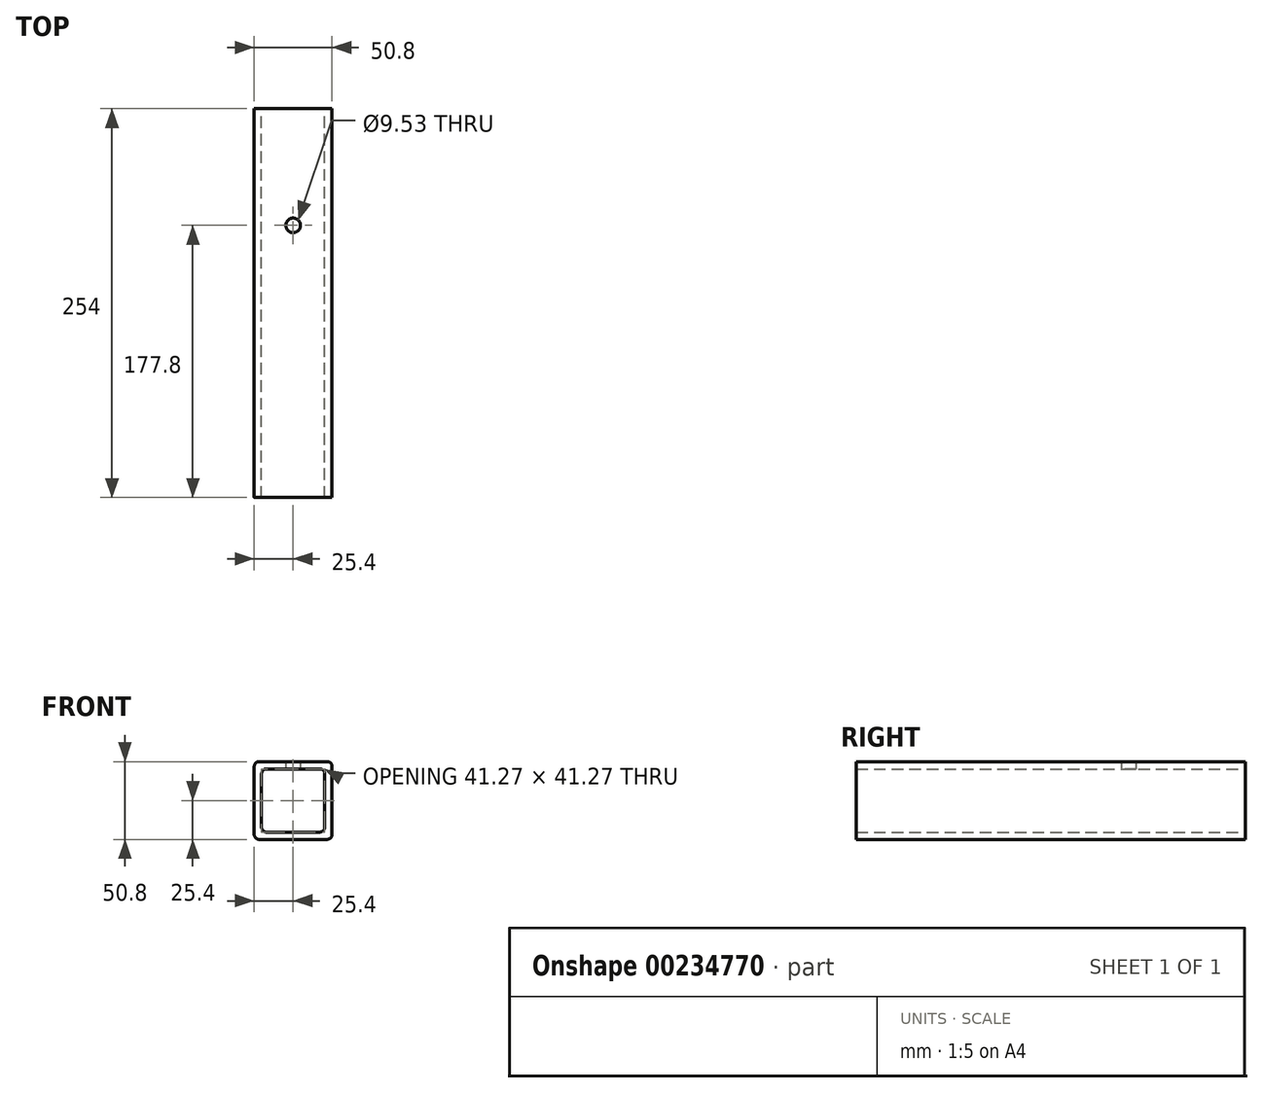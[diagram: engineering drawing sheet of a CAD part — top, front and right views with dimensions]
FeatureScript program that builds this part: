
annotation { "Feature Type Name" : "Feature", "Feature Type Description" : "" }
export const myFeature = defineFeature(function(context is Context, id is Id, definition is map)
    precondition{}
    {
        {
            var Q0;
            Q0=qCreatedBy(makeId("Front.planeOp"),FACE);
            var sketch = newSketch(context, id + "F0", { "sketchPlane" : qUnion([Q0])});
            skLineSegment(sketch, "E0.bottom", {"start": v(22.23, -25.4) * mm, "end": v(-22.23, -25.4) * mm});
            skLineSegment(sketch, "E0.top", {"start": v(22.23, 25.4) * mm, "end": v(-22.23, 25.4) * mm});
            skLineSegment(sketch, "E0.left", {"start": v(25.4, -22.23) * mm, "end": v(25.4, 22.23) * mm});
            skLineSegment(sketch, "E0.right", {"start": v(-25.4, -22.23) * mm, "end": v(-25.4, 22.23) * mm});
            skPoint(sketch, "E0.middle", {"position": v(0, 0) * mm});
            skLineSegment(sketch, "E1.bottom", {"start": v(17.46, -20.64) * mm, "end": v(-17.46, -20.64) * mm});
            skLineSegment(sketch, "E1.top", {"start": v(17.46, 20.64) * mm, "end": v(-17.46, 20.64) * mm});
            skLineSegment(sketch, "E1.left", {"start": v(20.64, -17.46) * mm, "end": v(20.64, 17.46) * mm});
            skLineSegment(sketch, "E1.right", {"start": v(-20.64, -17.46) * mm, "end": v(-20.64, 17.46) * mm});
            skPoint(sketch, "E2.visualSharp", {"position": v(-25.4, 25.4) * mm});
            skArc(sketch, "E2.filletArc", {"start": v(-22.23, 25.4) * mm, "mid": v(-24.47, 24.47) * mm, "end": v(-25.4, 22.23) * mm});
            skPoint(sketch, "E3.visualSharp", {"position": v(25.4, 25.4) * mm});
            skArc(sketch, "E3.filletArc", {"start": v(25.4, 22.23) * mm, "mid": v(24.47, 24.47) * mm, "end": v(22.23, 25.4) * mm});
            skPoint(sketch, "E4.visualSharp", {"position": v(20.64, 20.64) * mm});
            skArc(sketch, "E4.filletArc", {"start": v(20.64, 17.46) * mm, "mid": v(19.7, 19.7) * mm, "end": v(17.46, 20.64) * mm});
            skPoint(sketch, "E5.visualSharp", {"position": v(-20.64, 20.64) * mm});
            skArc(sketch, "E5.filletArc", {"start": v(-17.46, 20.64) * mm, "mid": v(-19.7, 19.7) * mm, "end": v(-20.64, 17.46) * mm});
            skPoint(sketch, "E6.visualSharp", {"position": v(-20.64, -20.64) * mm});
            skArc(sketch, "E6.filletArc", {"start": v(-20.64, -17.46) * mm, "mid": v(-19.7, -19.7) * mm, "end": v(-17.46, -20.64) * mm});
            skPoint(sketch, "E7.visualSharp", {"position": v(-25.4, -25.4) * mm});
            skArc(sketch, "E7.filletArc", {"start": v(-25.4, -22.23) * mm, "mid": v(-24.47, -24.47) * mm, "end": v(-22.23, -25.4) * mm});
            skPoint(sketch, "E8.visualSharp", {"position": v(20.64, -20.64) * mm});
            skArc(sketch, "E8.filletArc", {"start": v(17.46, -20.64) * mm, "mid": v(19.7, -19.7) * mm, "end": v(20.64, -17.46) * mm});
            skPoint(sketch, "E9.visualSharp", {"position": v(25.4, -25.4) * mm});
            skArc(sketch, "E9.filletArc", {"start": v(22.23, -25.4) * mm, "mid": v(24.47, -24.47) * mm, "end": v(25.4, -22.23) * mm});
            skSolve(sketch);
        }
        {
            var Q0;
            Q0=makeQuery(id+"F0.imprint","IMPRINT",FACE,{"disambiguationData":[TD([[makeQuery(id+"F0.imprint","IMPRINT",EDGE,{"derivedFrom":sQuery(id+"F0.wireOp",EDGE,"E0.bottom")}),-1.0]])]});
            extrude(context, id + "F3", {"entities" : qUnion([Q0]), "depth" : 254 * mm});
        }
        {
            var Q0;
            Q0=qCreatedBy(makeId("Top.planeOp"),FACE);
            var sketch = newSketch(context, id + "F1", { "sketchPlane" : qUnion([Q0])});
            skPoint(sketch, "E10", {"position": v(0, -76.2) * mm});
            skSolve(sketch);
        }
        {
            var Q0;
            Q0=sQuery(id+"F1.wireOp",VERTEX,"E10");
            var Q1;
            Q1=makeQuery(id+"F3.opExtrude","SWEPT_BODY",BODY,{"disambiguationData":[OSD([sQuery(id+"F0.wireOp",EDGE,"E0.bottom"),sQuery(id+"F0.wireOp",EDGE,"E0.top"),sQuery(id+"F0.wireOp",EDGE,"E0.left"),sQuery(id+"F0.wireOp",EDGE,"E0.right"),sQuery(id+"F0.wireOp",EDGE,"E1.bottom"),sQuery(id+"F0.wireOp",EDGE,"E1.top"),sQuery(id+"F0.wireOp",EDGE,"E1.left"),sQuery(id+"F0.wireOp",EDGE,"E1.right"),sQuery(id+"F0.wireOp",EDGE,"E2.filletArc"),sQuery(id+"F0.wireOp",EDGE,"E3.filletArc"),sQuery(id+"F0.wireOp",EDGE,"E4.filletArc"),sQuery(id+"F0.wireOp",EDGE,"E5.filletArc"),sQuery(id+"F0.wireOp",EDGE,"E6.filletArc"),sQuery(id+"F0.wireOp",EDGE,"E7.filletArc"),sQuery(id+"F0.wireOp",EDGE,"E8.filletArc"),sQuery(id+"F0.wireOp",EDGE,"E9.filletArc")])]});
            hole(context, id + "F2", {"style" : HoleStyle.SIMPLE, "endStyle" : HoleEndStyle.THROUGH, "oppositeDirection" : true, "holeDiameter" : 9.52 * mm, "locations" : qUnion([Q0]), "scope" : qUnion([Q1]), "isTappedThrough" : true});
        }
    });
